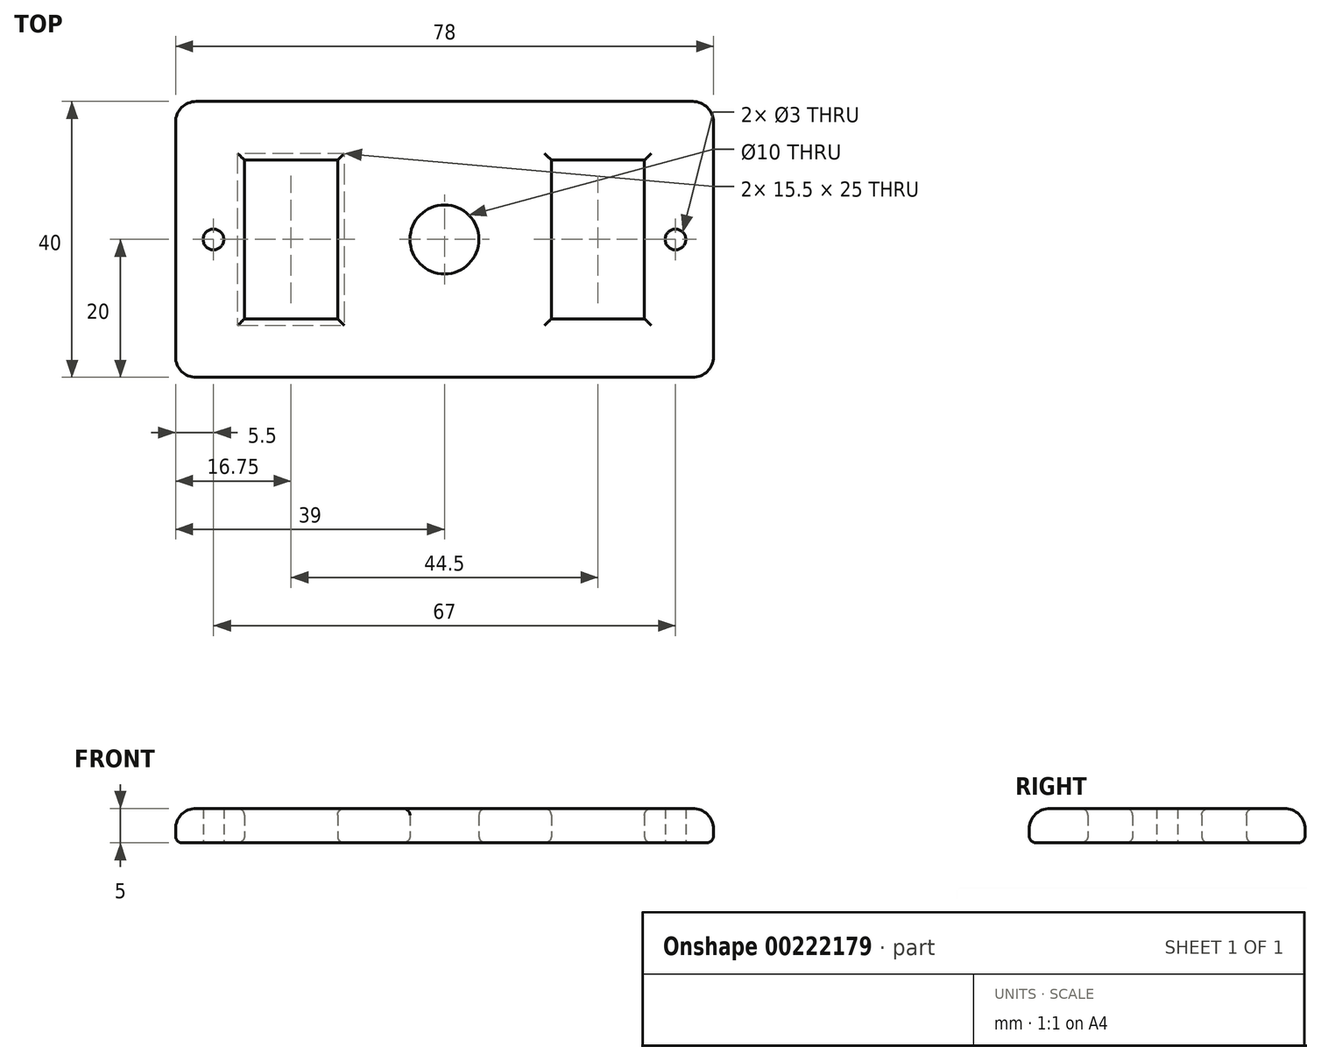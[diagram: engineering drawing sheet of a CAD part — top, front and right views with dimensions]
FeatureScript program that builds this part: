
annotation { "Feature Type Name" : "Feature", "Feature Type Description" : "" }
export const myFeature = defineFeature(function(context is Context, id is Id, definition is map)
    precondition{}
    {
        {
            var Q0;
            Q0=qCreatedBy(makeId("Top.planeOp"),FACE);
            var sketch = newSketch(context, id + "F0", { "sketchPlane" : qUnion([Q0])});
            skLineSegment(sketch, "E0.bottom", {"start": v(-39, 20) * mm, "end": v(0, 20) * mm});
            skLineSegment(sketch, "E0.top", {"start": v(-39, -20) * mm, "end": v(39, -20) * mm});
            skLineSegment(sketch, "E0.left", {"start": v(-39, 20) * mm, "end": v(-39, -20) * mm});
            skLineSegment(sketch, "E0.right", {"start": v(39, 20) * mm, "end": v(39, 0) * mm});
            skLineSegment(sketch, "E1", {"start": v(0, 73.35) * mm, "end": v(0, -33.35) * mm, "construction": true});
            skLineSegment(sketch, "E2", {"start": v(-40.36, 0) * mm, "end": v(118.36, 0) * mm, "construction": true});
            skLineSegment(sketch, "E3.bottom", {"start": v(-29, 11.5) * mm, "end": v(-15.5, 11.5) * mm});
            skLineSegment(sketch, "E3.top", {"start": v(-29, -11.5) * mm, "end": v(-15.5, -11.5) * mm});
            skLineSegment(sketch, "E3.left", {"start": v(-29, 11.5) * mm, "end": v(-29, -11.5) * mm});
            skLineSegment(sketch, "E3.right", {"start": v(-15.5, 11.5) * mm, "end": v(-15.5, -11.5) * mm});
            skLineSegment(sketch, "E4.MirrorCS", {"start": v(29, 11.5) * mm, "end": v(29, 0) * mm});
            skLineSegment(sketch, "E5.MirrorCS", {"start": v(29, 11.5) * mm, "end": v(15.5, 11.5) * mm});
            skLineSegment(sketch, "E6.MirrorCS", {"start": v(15.5, 11.5) * mm, "end": v(15.5, -11.5) * mm});
            skLineSegment(sketch, "E7.MirrorCS", {"start": v(29, -11.5) * mm, "end": v(15.5, -11.5) * mm});
            skCircle(sketch, "E8", {"center": v(-33.5, 0) * mm, "radius": 1.5 * mm});
            skCircle(sketch, "E9", {"center": v(0, 0) * mm, "radius": 5 * mm});
            skCircle(sketch, "E10.MirrorC", {"center": v(33.5, 0) * mm, "radius": 1.5 * mm});
            skLineSegment(sketch, "E11", {"start": v(0, 20) * mm, "end": v(39, 20) * mm});
            skLineSegment(sketch, "E12", {"start": v(39, 0) * mm, "end": v(39, -20) * mm});
            skLineSegment(sketch, "E13", {"start": v(29, 0) * mm, "end": v(29, -11.5) * mm});
            skSolve(sketch);
        }
        {
            var Q0;
            Q0=makeQuery(id+"F0.imprint","IMPRINT",FACE,{"disambiguationData":[TD([[makeQuery(id+"F0.imprint","IMPRINT",EDGE,{"derivedFrom":sQuery(id+"F0.wireOp",EDGE,"E0.bottom")}),-1.0]])]});
            extrude(context, id + "F1", {"entities" : qUnion([Q0]), "depth" : 5 * mm});
        }
        {
            var Q0;
            Q0=makeQuery(id+"F1.opExtrude","CAP_EDGE",EDGE,{"disambiguationData":[OSD([sQuery(id+"F0.wireOp",EDGE,"E0.bottom")])],"isStart":false});
            var Q1;
            Q1=makeQuery(id+"F1.opExtrude","CAP_EDGE",EDGE,{"disambiguationData":[OSD([sQuery(id+"F0.wireOp",EDGE,"E0.left")])],"isStart":false});
            var Q2;
            Q2=makeQuery(id+"F1.opExtrude","CAP_EDGE",EDGE,{"disambiguationData":[OSD([sQuery(id+"F0.wireOp",EDGE,"E0.top")])],"isStart":false});
            var Q3;
            Q3=makeQuery(id+"F1.opExtrude","CAP_EDGE",EDGE,{"disambiguationData":[OSD([sQuery(id+"F0.wireOp",EDGE,"E0.right")])],"isStart":false});
            var Q4;
            Q4=makeQuery(id+"F1.opExtrude","SWEPT_EDGE",EDGE,{"disambiguationData":[OSD([sQuery(id+"F0.wireOp",EDGE,"E0.top"),sQuery(id+"F0.wireOp",EDGE,"E0.left")])]});
            var Q5;
            Q5=makeQuery(id+"F1.opExtrude","SWEPT_EDGE",EDGE,{"disambiguationData":[OSD([sQuery(id+"F0.wireOp",EDGE,"E0.bottom"),sQuery(id+"F0.wireOp",EDGE,"E0.left")])]});
            var Q6;
            Q6=makeQuery(id+"F1.opExtrude","SWEPT_EDGE",EDGE,{"disambiguationData":[OSD([sQuery(id+"F0.wireOp",EDGE,"E0.right"),sQuery(id+"F0.wireOp",EDGE,"E11")])]});
            var Q7;
            Q7=makeQuery(id+"F1.opExtrude","SWEPT_EDGE",EDGE,{"disambiguationData":[OSD([sQuery(id+"F0.wireOp",EDGE,"E0.top"),sQuery(id+"F0.wireOp",EDGE,"E12")])]});
            fillet(context, id + "F2", {"entities" : qUnion([Q0, Q1, Q2, Q3, Q4, Q5, Q6, Q7]), "radius" : 3 * mm, "tangentPropagation" : true, "allowEdgeOverflow" : false});
        }
        {
            var Q0;
            Q0=makeQuery(id+"F1.opExtrude","CAP_EDGE",EDGE,{"disambiguationData":[OSD([sQuery(id+"F0.wireOp",EDGE,"E0.top")])],"isStart":true});
            fillet(context, id + "F3", {"entities" : qUnion([Q0]), "radius" : 1 * mm, "tangentPropagation" : true, "allowEdgeOverflow" : false});
        }
        {
            var Q0;
            Q0=makeQuery(id+"F1.opExtrude","CAP_EDGE",EDGE,{"disambiguationData":[OSD([sQuery(id+"F0.wireOp",EDGE,"E3.top")])],"isStart":false});
            var Q1;
            Q1=makeQuery(id+"F1.opExtrude","CAP_EDGE",EDGE,{"disambiguationData":[OSD([sQuery(id+"F0.wireOp",EDGE,"E3.right")])],"isStart":false});
            var Q2;
            Q2=makeQuery(id+"F1.opExtrude","CAP_EDGE",EDGE,{"disambiguationData":[OSD([sQuery(id+"F0.wireOp",EDGE,"E3.bottom")])],"isStart":false});
            var Q3;
            Q3=makeQuery(id+"F1.opExtrude","CAP_EDGE",EDGE,{"disambiguationData":[OSD([sQuery(id+"F0.wireOp",EDGE,"E3.left")])],"isStart":false});
            var Q4;
            Q4=makeQuery(id+"F1.opExtrude","CAP_EDGE",EDGE,{"disambiguationData":[OSD([sQuery(id+"F0.wireOp",EDGE,"E6.MirrorCS")])],"isStart":false});
            var Q5;
            Q5=makeQuery(id+"F1.opExtrude","CAP_EDGE",EDGE,{"disambiguationData":[OSD([sQuery(id+"F0.wireOp",EDGE,"E5.MirrorCS")])],"isStart":false});
            var Q6;
            Q6=makeQuery(id+"F1.opExtrude","CAP_EDGE",EDGE,{"disambiguationData":[OSD([sQuery(id+"F0.wireOp",EDGE,"E4.MirrorCS"),sQuery(id+"F0.wireOp",EDGE,"E13")])],"isStart":false});
            var Q7;
            Q7=makeQuery(id+"F1.opExtrude","CAP_EDGE",EDGE,{"disambiguationData":[OSD([sQuery(id+"F0.wireOp",EDGE,"E7.MirrorCS")])],"isStart":false});
            var Q8;
            Q8=makeQuery(id+"F1.opExtrude","CAP_EDGE",EDGE,{"disambiguationData":[OSD([sQuery(id+"F0.wireOp",EDGE,"E3.left")])],"isStart":true});
            var Q9;
            Q9=makeQuery(id+"F1.opExtrude","CAP_EDGE",EDGE,{"disambiguationData":[OSD([sQuery(id+"F0.wireOp",EDGE,"E3.right")])],"isStart":true});
            var Q10;
            Q10=makeQuery(id+"F1.opExtrude","CAP_EDGE",EDGE,{"disambiguationData":[OSD([sQuery(id+"F0.wireOp",EDGE,"E3.bottom")])],"isStart":true});
            var Q11;
            Q11=makeQuery(id+"F1.opExtrude","CAP_EDGE",EDGE,{"disambiguationData":[OSD([sQuery(id+"F0.wireOp",EDGE,"E3.top")])],"isStart":true});
            var Q12;
            Q12=makeQuery(id+"F1.opExtrude","CAP_EDGE",EDGE,{"disambiguationData":[OSD([sQuery(id+"F0.wireOp",EDGE,"E7.MirrorCS")])],"isStart":true});
            var Q13;
            Q13=makeQuery(id+"F1.opExtrude","CAP_EDGE",EDGE,{"disambiguationData":[OSD([sQuery(id+"F0.wireOp",EDGE,"E4.MirrorCS"),sQuery(id+"F0.wireOp",EDGE,"E13")])],"isStart":true});
            var Q14;
            Q14=makeQuery(id+"F1.opExtrude","CAP_EDGE",EDGE,{"disambiguationData":[OSD([sQuery(id+"F0.wireOp",EDGE,"E5.MirrorCS")])],"isStart":true});
            var Q15;
            Q15=makeQuery(id+"F1.opExtrude","CAP_EDGE",EDGE,{"disambiguationData":[OSD([sQuery(id+"F0.wireOp",EDGE,"E6.MirrorCS")])],"isStart":true});
            var Q16;
            Q16=makeQuery(id+"F1.opExtrude","CAP_EDGE",EDGE,{"disambiguationData":[OSD([sQuery(id+"F0.wireOp",EDGE,"E9")])],"isStart":false});
            var Q17;
            Q17=makeQuery(id+"F1.opExtrude","CAP_EDGE",EDGE,{"disambiguationData":[OSD([sQuery(id+"F0.wireOp",EDGE,"E9")])],"isStart":true});
            fillet(context, id + "F4", {"entities" : qUnion([Q0, Q1, Q2, Q3, Q4, Q5, Q6, Q7, Q8, Q9, Q10, Q11, Q12, Q13, Q14, Q15, Q16, Q17]), "radius" : 1 * mm, "tangentPropagation" : true, "allowEdgeOverflow" : false});
        }
    });
